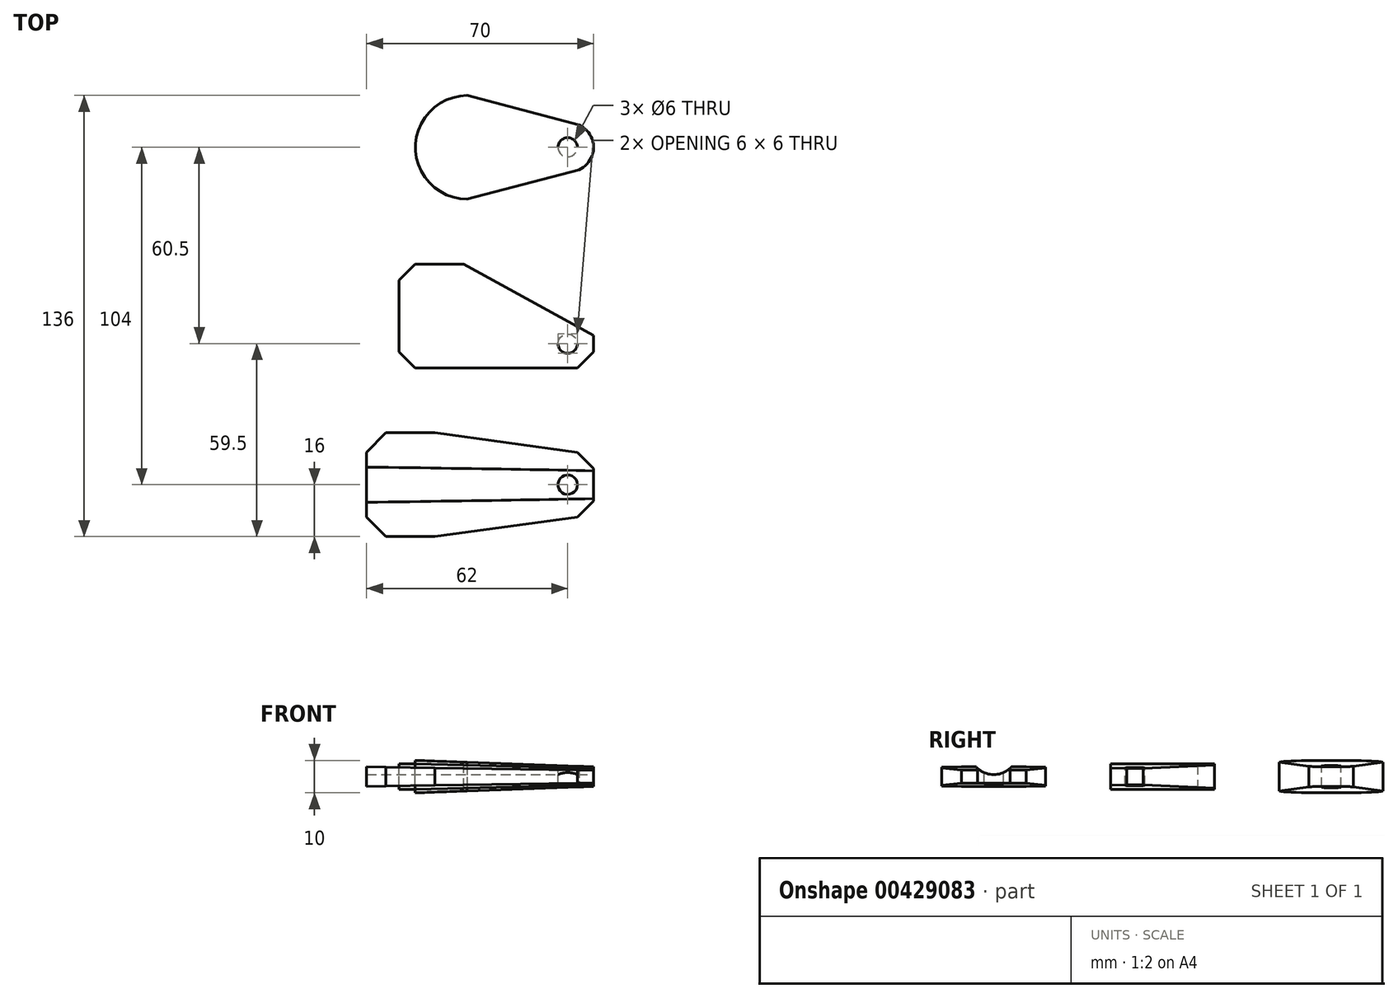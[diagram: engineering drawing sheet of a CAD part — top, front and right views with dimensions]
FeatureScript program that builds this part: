
annotation { "Feature Type Name" : "Feature", "Feature Type Description" : "" }
export const myFeature = defineFeature(function(context is Context, id is Id, definition is map)
    precondition{}
    {
        {
            var Q0;
            Q0=qCreatedBy(makeId("Front.planeOp"),FACE);
            var sketch = newSketch(context, id + "F0", { "sketchPlane" : qUnion([Q0])});
            skLineSegment(sketch, "E0", {"start": v(0, 0) * mm, "end": v(-70, 0) * mm, "construction": true});
            skLineSegment(sketch, "E1", {"start": v(-70, 3) * mm, "end": v(-70, 0) * mm, "construction": true});
            skLineSegment(sketch, "E2", {"start": v(-70, -3) * mm, "end": v(-70, 0) * mm, "construction": true});
            skLineSegment(sketch, "E3", {"start": v(0, 2) * mm, "end": v(-70, 3) * mm});
            skLineSegment(sketch, "E4", {"start": v(-70, 3) * mm, "end": v(-70, -3) * mm});
            skLineSegment(sketch, "E5", {"start": v(0, -2) * mm, "end": v(-70, -3) * mm});
            skLineSegment(sketch, "E6", {"start": v(0, -2) * mm, "end": v(0, 2) * mm});
            skSolve(sketch);
        }
        {
            var Q0;
            Q0=makeQuery(id+"F0.imprint","IMPRINT",FACE,{"disambiguationData":[TD([[makeQuery(id+"F0.imprint","IMPRINT",EDGE,{"derivedFrom":sQuery(id+"F0.wireOp",EDGE,"E3")}),1.0]])]});
            extrude(context, id + "F1", {"entities" : qUnion([Q0]), "depth" : 32 * mm});
        }
        {
            var Q0;
            Q0=qCreatedBy(makeId("Top.planeOp"),FACE);
            var sketch = newSketch(context, id + "F2", { "sketchPlane" : qUnion([Q0])});
            skLineSegment(sketch, "E7", {"start": v(0, 0) * mm, "end": v(0, -16) * mm, "construction": true});
            skLineSegment(sketch, "E8", {"start": v(0, -16) * mm, "end": v(-70, -16) * mm, "construction": true});
            skLineSegment(sketch, "E9", {"start": v(-64, -32) * mm, "end": v(-70, -26) * mm});
            skLineSegment(sketch, "E10", {"start": v(-70, -16) * mm, "end": v(-70, -26) * mm});
            skLineSegment(sketch, "E11", {"start": v(-49, -32) * mm, "end": v(-5, -26) * mm});
            skLineSegment(sketch, "E12", {"start": v(-5, -26) * mm, "end": v(0, -21) * mm});
            skPoint(sketch, "E13.orphan", {"position": v(0, -32) * mm});
            skLineSegment(sketch, "E14", {"start": v(-70, -26) * mm, "end": v(-70, -32) * mm});
            skLineSegment(sketch, "E15", {"start": v(-70, -32) * mm, "end": v(-64, -32) * mm});
            skLineSegment(sketch, "E16", {"start": v(-49, -32) * mm, "end": v(0, -32) * mm});
            skLineSegment(sketch, "E17", {"start": v(0, -21) * mm, "end": v(0, -32) * mm});
            skLineSegment(sketch, "E18.MirrorCS", {"start": v(-5, -6) * mm, "end": v(0, -11) * mm});
            skLineSegment(sketch, "E19.MirrorCS", {"start": v(0, -11) * mm, "end": v(0, 0) * mm});
            skLineSegment(sketch, "E20.MirrorCS", {"start": v(-49, 0) * mm, "end": v(0, 0) * mm});
            skLineSegment(sketch, "E21.MirrorCS", {"start": v(-49, 0) * mm, "end": v(-5, -6) * mm});
            skLineSegment(sketch, "E22.MirrorCS", {"start": v(-70, 0) * mm, "end": v(-64, 0) * mm});
            skLineSegment(sketch, "E23.MirrorCS", {"start": v(-64, 0) * mm, "end": v(-70, -6) * mm});
            skLineSegment(sketch, "E24.MirrorCS", {"start": v(-70, -6) * mm, "end": v(-70, 0) * mm});
            skLineSegment(sketch, "E25", {"start": v(0, -16) * mm, "end": v(-8, -16) * mm, "construction": true});
            skCircle(sketch, "E26", {"center": v(-8, -16) * mm, "radius": 3 * mm});
            skSolve(sketch);
        }
        {
            var Q0;
            Q0 = qSketchRegion(id + "F2", true);
            extrude(context, id + "F3", {"entities" : qUnion([Q0]), "operationType" : NewBodyOperationType.REMOVE, "endBound" : BoundingType.SYMMETRIC, "oppositeDirection" : true, "depth" : 25 * mm});
        }
        {
            var Q0;
            Q0=qCreatedBy(makeId("Right.planeOp"),FACE);
            var sketch = newSketch(context, id + "F4", { "sketchPlane" : qUnion([Q0])});
            skLineSegment(sketch, "E27", {"start": v(0, 0) * mm, "end": v(-16, 0) * mm, "construction": true});
            skLineSegment(sketch, "E28", {"start": v(-16, 0) * mm, "end": v(-16, 2) * mm, "construction": true});
            skLineSegment(sketch, "E29", {"start": v(-16, 2) * mm, "end": v(-16, 4) * mm, "construction": true});
            skPoint(sketch, "E29.endSnap0", {"position": v(-16, 1) * mm});
            skLineSegment(sketch, "E30", {"start": v(-16, 4) * mm, "end": v(-16, 6) * mm, "construction": true});
            skLineSegment(sketch, "E31", {"start": v(-16, 6) * mm, "end": v(-16, 8) * mm, "construction": true});
            skCircle(sketch, "E32", {"center": v(-16, 8) * mm, "radius": 7.38 * mm});
            skSolve(sketch);
        }
        {
            var Q0;
            Q0 = qSketchRegion(id + "F4", true);
            extrude(context, id + "F5", {"entities" : qUnion([Q0]), "operationType" : NewBodyOperationType.REMOVE, "oppositeDirection" : true, "depth" : 72.3 * mm});
        }
        {
            var Q0;
            Q0=qCreatedBy(makeId("Front.planeOp"),FACE);
            cPlane(context, id + "F6", {"entities" : qUnion([Q0]), "cplaneType" : CPlaneType.OFFSET, "offset" : 20 * mm, "oppositeDirection" : true, "width" : 150 * mm, "height" : 150 * mm});
        }
        {
            var Q0;
            Q0=qCreatedBy(id+"F6.planeOp",FACE);
            var sketch = newSketch(context, id + "F7", { "sketchPlane" : qUnion([Q0])});
            skLineSegment(sketch, "E33", {"start": v(0, 2.5) * mm, "end": v(0, 0) * mm, "construction": true});
            skLineSegment(sketch, "E34", {"start": v(0, 0) * mm, "end": v(0, -2.5) * mm, "construction": true});
            skLineSegment(sketch, "E35", {"start": v(0, 0) * mm, "end": v(-60, 0) * mm, "construction": true});
            skLineSegment(sketch, "E36", {"start": v(-60, 0) * mm, "end": v(-60, -4) * mm, "construction": true});
            skLineSegment(sketch, "E37", {"start": v(-60, 0) * mm, "end": v(-60, 4) * mm, "construction": true});
            skLineSegment(sketch, "E38", {"start": v(-60, 4) * mm, "end": v(-60, -4) * mm});
            skLineSegment(sketch, "E39", {"start": v(-60, -4) * mm, "end": v(0, -2.5) * mm});
            skLineSegment(sketch, "E40", {"start": v(0, -2.5) * mm, "end": v(0, 2.5) * mm});
            skLineSegment(sketch, "E41", {"start": v(0, 2.5) * mm, "end": v(-60, 4) * mm});
            skSolve(sketch);
        }
        {
            var Q0;
            Q0 = qSketchRegion(id + "F7", true);
            extrude(context, id + "F8", {"entities" : qUnion([Q0]), "oppositeDirection" : true, "depth" : 32 * mm});
        }
        {
            var Q0;
            Q0=qCreatedBy(makeId("Top.planeOp"),FACE);
            var sketch = newSketch(context, id + "F9", { "sketchPlane" : qUnion([Q0])});
            skLineSegment(sketch, "E42", {"start": v(0, 0) * mm, "end": v(0, 20) * mm, "construction": true});
            skLineSegment(sketch, "E43", {"start": v(0, 25) * mm, "end": v(0, 20) * mm, "construction": true});
            skLineSegment(sketch, "E44", {"start": v(0, 25) * mm, "end": v(0, 30) * mm, "construction": true});
            skLineSegment(sketch, "E45", {"start": v(0, 30) * mm, "end": v(0, 52) * mm, "construction": true});
            skLineSegment(sketch, "E46", {"start": v(0, 52) * mm, "end": v(-60, 52) * mm, "construction": true});
            skLineSegment(sketch, "E47", {"start": v(-60, 52) * mm, "end": v(-55, 52) * mm, "construction": true});
            skLineSegment(sketch, "E48", {"start": v(-60, 52) * mm, "end": v(-60, 47) * mm, "construction": true});
            skLineSegment(sketch, "E49", {"start": v(-60, 47) * mm, "end": v(-60, 25) * mm, "construction": true});
            skLineSegment(sketch, "E50", {"start": v(-60, 25) * mm, "end": v(-60, 20) * mm, "construction": true});
            skLineSegment(sketch, "E51", {"start": v(-60, 20) * mm, "end": v(-55, 20) * mm, "construction": true});
            skLineSegment(sketch, "E52", {"start": v(-55, 20) * mm, "end": v(-5, 20) * mm, "construction": true});
            skLineSegment(sketch, "E53", {"start": v(-5, 20) * mm, "end": v(0, 20) * mm, "construction": true});
            skLineSegment(sketch, "E54", {"start": v(0, 25) * mm, "end": v(-5, 20) * mm});
            skLineSegment(sketch, "E55", {"start": v(-5, 20) * mm, "end": v(0, 20) * mm});
            skLineSegment(sketch, "E56", {"start": v(0, 20) * mm, "end": v(0, 25) * mm});
            skLineSegment(sketch, "E57", {"start": v(-55, 20) * mm, "end": v(-60, 25) * mm});
            skLineSegment(sketch, "E58", {"start": v(-60, 25) * mm, "end": v(-60, 20) * mm});
            skLineSegment(sketch, "E59", {"start": v(-60, 20) * mm, "end": v(-55, 20) * mm});
            skLineSegment(sketch, "E60", {"start": v(-60, 47) * mm, "end": v(-55, 52) * mm});
            skLineSegment(sketch, "E61", {"start": v(-55, 52) * mm, "end": v(-60, 52) * mm});
            skLineSegment(sketch, "E62", {"start": v(-60, 52) * mm, "end": v(-60, 47) * mm});
            skLineSegment(sketch, "E63", {"start": v(-55, 52) * mm, "end": v(-40, 52) * mm, "construction": true});
            skLineSegment(sketch, "E64", {"start": v(0, 30) * mm, "end": v(-40, 52) * mm});
            skLineSegment(sketch, "E65", {"start": v(-40, 52) * mm, "end": v(0, 52) * mm});
            skLineSegment(sketch, "E66", {"start": v(0, 52) * mm, "end": v(0, 30) * mm});
            skLineSegment(sketch, "E67", {"start": v(0, 20) * mm, "end": v(0, 27.5) * mm, "construction": true});
            skLineSegment(sketch, "E68", {"start": v(0, 27.5) * mm, "end": v(-8, 27.5) * mm, "construction": true});
            skCircle(sketch, "E69", {"center": v(-8, 27.5) * mm, "radius": 3 * mm});
            skSolve(sketch);
        }
        {
            var Q0;
            Q0 = qSketchRegion(id + "F9", true);
            extrude(context, id + "F10", {"entities" : qUnion([Q0]), "operationType" : NewBodyOperationType.REMOVE, "endBound" : BoundingType.SYMMETRIC, "oppositeDirection" : true, "depth" : 25 * mm});
        }
        {
            var Q0;
            Q0=qCreatedBy(id+"F6.planeOp",FACE);
            cPlane(context, id + "F11", {"entities" : qUnion([Q0]), "cplaneType" : CPlaneType.OFFSET, "offset" : 52 * mm, "oppositeDirection" : true, "width" : 150 * mm, "height" : 150 * mm});
        }
        {
            var Q0;
            Q0=qCreatedBy(id+"F11.planeOp",FACE);
            var sketch = newSketch(context, id + "F12", { "sketchPlane" : qUnion([Q0])});
            skLineSegment(sketch, "E70", {"start": v(0, -3) * mm, "end": v(0, 0) * mm});
            skLineSegment(sketch, "E71", {"start": v(0, 3) * mm, "end": v(0, 0) * mm});
            skLineSegment(sketch, "E72", {"start": v(0, 0) * mm, "end": v(-55, 0) * mm, "construction": true});
            skLineSegment(sketch, "E73", {"start": v(-55, 0) * mm, "end": v(-55, 5) * mm, "construction": true});
            skLineSegment(sketch, "E74", {"start": v(-55, 0) * mm, "end": v(-55, -5) * mm, "construction": true});
            skLineSegment(sketch, "E75", {"start": v(-55, -5) * mm, "end": v(-55, 5) * mm});
            skLineSegment(sketch, "E76", {"start": v(-55, 5) * mm, "end": v(0, 3) * mm});
            skLineSegment(sketch, "E77", {"start": v(0, -3) * mm, "end": v(-55, -5) * mm});
            skSolve(sketch);
        }
        {
            var Q0;
            Q0 = qSketchRegion(id + "F12", true);
            var Q1;
            Q1 = qConstructionFilter(qBodyType(qCreatedBy(id + "F12" ,EDGE), BodyType.WIRE), ConstructionObject.NO);
            extrude(context, id + "F13", {"entities" : qUnion([Q0]), "surfaceEntities" : qUnion([Q1]), "oppositeDirection" : true, "depth" : 32 * mm});
        }
        {
            var Q0;
            Q0=qCreatedBy(makeId("Top.planeOp"),FACE);
            var sketch = newSketch(context, id + "F14", { "sketchPlane" : qUnion([Q0])});
            skLineSegment(sketch, "E78", {"start": v(0, 0) * mm, "end": v(0, 72) * mm, "construction": true});
            skLineSegment(sketch, "E79", {"start": v(0, 72) * mm, "end": v(0, 88) * mm, "construction": true});
            skLineSegment(sketch, "E80", {"start": v(0, 88) * mm, "end": v(0, 104) * mm, "construction": true});
            skLineSegment(sketch, "E81", {"start": v(0, 88) * mm, "end": v(-55, 88) * mm, "construction": true});
            skLineSegment(sketch, "E82", {"start": v(-39, 104) * mm, "end": v(-39, 72) * mm, "construction": true});
            skLineSegment(sketch, "E83", {"start": v(0, 88) * mm, "end": v(-7.5, 88) * mm, "construction": true});
            skLineSegment(sketch, "E84", {"start": v(-7.5, 88) * mm, "end": v(-8, 88) * mm, "construction": true});
            skLineSegment(sketch, "E85", {"start": v(-7.5, 95.5) * mm, "end": v(-7.5, 88) * mm, "construction": true});
            skLineSegment(sketch, "E86", {"start": v(-7.5, 88) * mm, "end": v(-7.5, 80.5) * mm, "construction": true});
            skArc(sketch, "E87", {"start": v(-7.5, 80.5) * mm, "mid": v(-7.1, 80.51) * mm, "end": v(-6.7, 80.54) * mm});
            skArc(sketch, "E88", {"start": v(-55, 88) * mm, "mid": v(-50.31, 76.69) * mm, "end": v(-39, 72) * mm});
            skLineSegment(sketch, "E89", {"start": v(0, 88) * mm, "end": v(-4.5, 88) * mm, "construction": true});
            skLineSegment(sketch, "E90", {"start": v(-4.5, 88) * mm, "end": v(-4.5, 94.87) * mm, "construction": true});
            skLineSegment(sketch, "E91", {"start": v(-4.5, 88) * mm, "end": v(-4.5, 81.13) * mm, "construction": true});
            skLineSegment(sketch, "E92", {"start": v(-4.5, 94.87) * mm, "end": v(-6.7, 95.46) * mm});
            skLineSegment(sketch, "E93", {"start": v(-6.7, 80.54) * mm, "end": v(-4.5, 81.13) * mm});
            skPoint(sketch, "E94.end.orphan", {"position": v(-55, 104) * mm});
            skLineSegment(sketch, "E95", {"start": v(-55, 104) * mm, "end": v(-39, 104) * mm});
            skLineSegment(sketch, "E96", {"start": v(-39, 104) * mm, "end": v(0, 104) * mm});
            skLineSegment(sketch, "E97", {"start": v(0, 104) * mm, "end": v(0, 88) * mm});
            skLineSegment(sketch, "E98", {"start": v(-39, 72) * mm, "end": v(-55, 72) * mm, "construction": true});
            skLineSegment(sketch, "E99", {"start": v(-55, 72) * mm, "end": v(-39, 72) * mm});
            skLineSegment(sketch, "E100", {"start": v(-39, 72) * mm, "end": v(0, 72) * mm});
            skLineSegment(sketch, "E101", {"start": v(0, 88) * mm, "end": v(0, 72) * mm});
            skArc(sketch, "E102.trimOffspring", {"start": v(-4.5, 81.13) * mm, "mid": v(0, 88) * mm, "end": v(-4.5, 94.87) * mm});
            skArc(sketch, "E103.trimOffspring", {"start": v(-6.7, 95.46) * mm, "mid": v(-7.1, 95.49) * mm, "end": v(-7.5, 95.5) * mm});
            skLineSegment(sketch, "E104", {"start": v(-39, 104) * mm, "end": v(-6.7, 95.46) * mm});
            skLineSegment(sketch, "E105", {"start": v(-6.7, 80.54) * mm, "end": v(-39, 72) * mm});
            skSolve(sketch);
        }
        {
            var Q0;
            Q0 = qSketchRegion(id + "F14", true);
            extrude(context, id + "F15", {"entities" : qUnion([Q0]), "operationType" : NewBodyOperationType.REMOVE, "endBound" : BoundingType.SYMMETRIC, "depth" : 80 * mm});
        }
        {
            var Q0;
            Q0=qCreatedBy(makeId("Top.planeOp"),FACE);
            var sketch = newSketch(context, id + "F16", { "sketchPlane" : qUnion([Q0])});
            skLineSegment(sketch, "E106", {"start": v(0, 0) * mm, "end": v(0, 20) * mm, "construction": true});
            skLineSegment(sketch, "E107", {"start": v(0, 20) * mm, "end": v(0, 52) * mm, "construction": true});
            skLineSegment(sketch, "E108", {"start": v(0, 52) * mm, "end": v(0, 72) * mm, "construction": true});
            skLineSegment(sketch, "E109", {"start": v(0, 72) * mm, "end": v(0, 88) * mm, "construction": true});
            skLineSegment(sketch, "E110", {"start": v(0, 88) * mm, "end": v(-55, 88) * mm, "construction": true});
            skLineSegment(sketch, "E111", {"start": v(-55, 88) * mm, "end": v(-39, 88) * mm, "construction": true});
            skLineSegment(sketch, "E112", {"start": v(-39, 88) * mm, "end": v(-39, 104) * mm, "construction": true});
            skLineSegment(sketch, "E113", {"start": v(-39, 88) * mm, "end": v(-39, 72) * mm, "construction": true});
            skArc(sketch, "E114", {"start": v(-39, 104) * mm, "mid": v(-55, 88) * mm, "end": v(-39, 72) * mm});
            skLineSegment(sketch, "E115", {"start": v(-39, 104) * mm, "end": v(-55, 104) * mm});
            skLineSegment(sketch, "E116", {"start": v(-55, 104) * mm, "end": v(-55, 72) * mm});
            skLineSegment(sketch, "E117", {"start": v(-55, 72) * mm, "end": v(-39, 72) * mm});
            skLineSegment(sketch, "E118", {"start": v(0, 88) * mm, "end": v(-8, 88) * mm, "construction": true});
            skCircle(sketch, "E119", {"center": v(-8, 88) * mm, "radius": 3 * mm});
            skSolve(sketch);
        }
        {
            var Q0;
            Q0 = qSketchRegion(id + "F16", true);
            extrude(context, id + "F17", {"entities" : qUnion([Q0]), "operationType" : NewBodyOperationType.REMOVE, "endBound" : BoundingType.SYMMETRIC, "oppositeDirection" : true, "depth" : 25 * mm});
        }
    });
